# Revit family: 01-9949-13 LLAVE EXTENSION MANGUERA METAL SATIN
name_source: partatom
category: Aparatos sanitarios
units: mm (PartAtom-declared; Revit-internal decimal feet)

## family parameters
Anfitrión = Cara
Compartido = No
Corte con vacíos al cargar = No
Cota de conector redondo = Diámetro de uso
Número OmniClass = 23.31.11.00
Punto de cálculo de habitación = No
Tipo de pieza = Normal

## types (1)
- 01-9949-13
    Acometida = Dim 1/2" NPT
    Alto = 98 mm  [stored 0.321522 ft]
    Ancho = 163 mm
    Ancho manija llave = 60 mm  [stored 0.19685 ft]
    Conexión AC = Sí
    Conexión AF = Sí
    Conexión de residuos = No
    Conexión de ventilación = No
    Descripción = Llave jardin
    Dim Escudo = 60 mm  [stored 0.19685 ft]
    Elevación por defecto = 0 mm  [stored 0 ft]
    Fabricante = Gricol
    Imagen de tipo = LLAVE EXTENSION MANGUERA METAL SATIN.jpg
    Link Ficha Tecnica = http://infotecnica.gricol.com
    Metal - Zamak satinado = Metal Zamak Satinado
    Metal Laton Satinado = Metal Laton satinado gris
    Modelo = 01-9949-13
    Product Name = LLAVE EXTENSION MANGUERA METAL SATIN
    Salida = Dim 3/4" NH
    URL = https://www.gricol.com

note: [stored X ft] marks values corroborated as IEEE doubles in the binary element streams (Revit-internal decimal feet)

## geometry (parser evidence)
native form markers: Blend x2, Sweep x4
no freeform markers — native parametric forms only
